# Revit family: ISI_IdealStandard_WallHungWashBasins_Tempo-60cm_E0668 (IS_Tempo_E0668_BIM_GB)
name_source: partatom
category: Plumbing Fixtures
revit_build: Autodesk Revit MEP 2014 (Build: 20130308_1515(x64)
units: mm (PartAtom-declared; Revit-internal decimal feet)

## types (1)
- E0668 - Tempo 60cm Vanity furniture washbasin, with overflow - one taphole
    Accessories = www.idealspec.co.uk
    AreaUnits = millimeters
    Assembly Code = C1030200
    AssetType = Fixed
    BIMObjectName = ISI_IdealStandard_WallHungWashBasins_Tempo-60 cm_E0668
    Brand = Ideal Standard
    CWFU = 0
    Category = Plumbing
    Color = White
    ConnectionType = Plumbing
    Cost = 0 $
    Default Elevation = 800 mm  [stored 2.62467 ft]
    Description = Tempo 60 cm vanity furniture washbasin, with overflow - one taphole
    DrainSize = 32 mm  [stored 0.104987 ft]
    DurationUnit = year
    ECA = No
    ExpectedLife = 30
    Features = 60 cm vanity washbasin, with overflow - one taphole
    Finish = White
    HWFU = 0
    IfcExportAs = IfcSanitaryTerminalType
    IfcExportType = WASHHANDBASIN
    InstallationInstructions = www.idealspec.co.uk/resources.html
    LinearUnits = millimeters
    ManufacturerURL = www.idealspec.co.uk
    Material = Vitreous china
    Model = E066801
    ModelNumber = E066801
    ModelReference = Tempo 60 cm vanity furniture washbasin, with overflow - one taphole
    NBSDescription = Pedestal wash basins
    NBSReference = 45-35-70/365
    Name = WallHungWashBasins_Tempo-60cm_E0668_IdealStandard
    NettWeight = 11.8 Kg
    NominalDepth = 450 mm
    NominalHeight = 138 mm
    NominalLength = 450 mm
    NominalWidth = 608 mm
    ProductInformation = www.idealspec.co.uk/assets/datasheet/E066801
    Shape = Rectangular
    Size = 608 x 450 x 138 mm
    Space = Internal
    SpareParts = www.fastpart-spares.co.uk
    URL = www.idealspec.co.uk
    Uniclass2015Description = Counter top wash basins
    Uniclass2015Reference = Pr_40_20_96_18
    Uniclass2015Version = Products v1.1
    Version = 2
    VolumeUnits = Litres
    WFU = 0
    WRAS = No
    WarrantyDescription = Manufacturers Warranty
    WarrantyDurationParts = 99
    WarrantyDurationUnit = year
    WashHandBasinMounting = CounterTop
    WashHandBasinType = HandRinse
    WaterEfficientProduct = No

note: [stored X ft] marks values corroborated as IEEE doubles in the binary element streams (Revit-internal decimal feet)

## geometry (parser evidence)
native form markers: Sweep x9
no freeform markers — native parametric forms only
